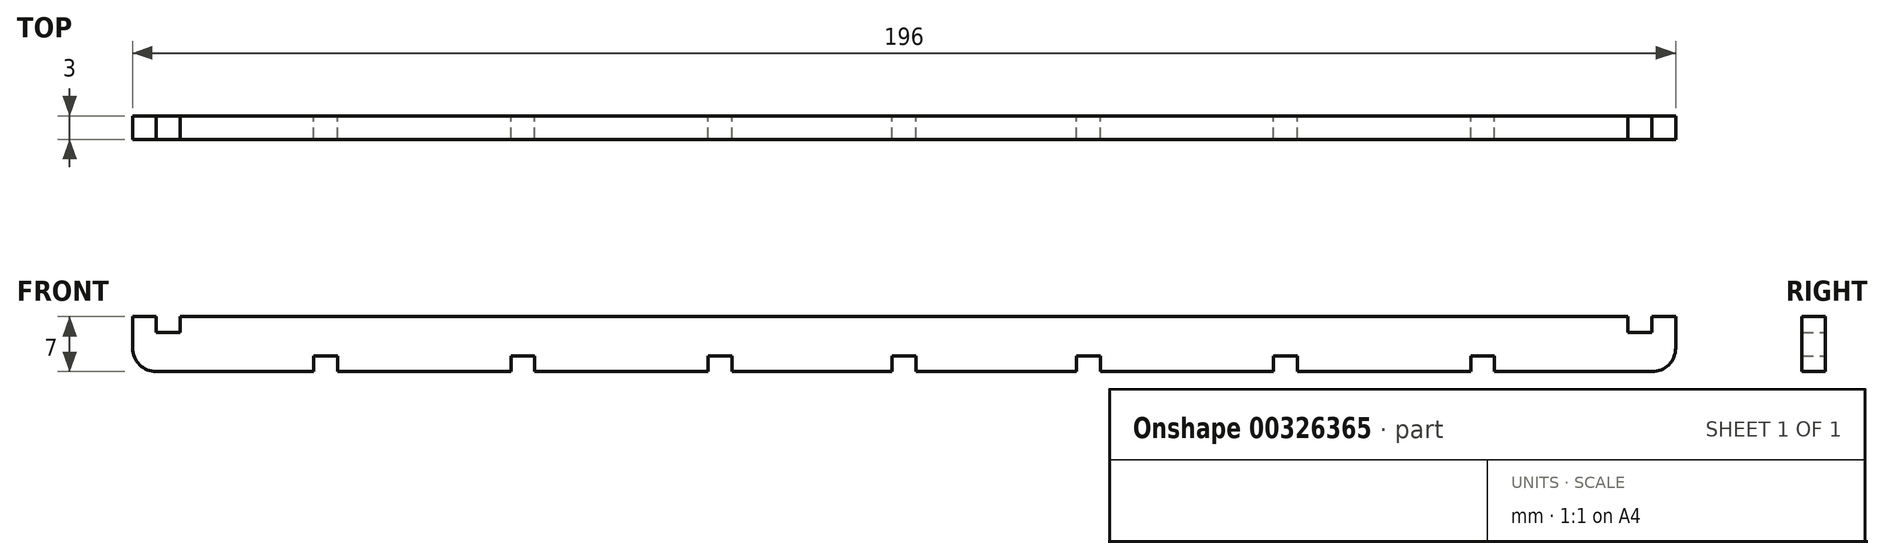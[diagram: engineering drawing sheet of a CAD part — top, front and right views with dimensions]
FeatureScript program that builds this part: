
annotation { "Feature Type Name" : "Feature", "Feature Type Description" : "" }
export const myFeature = defineFeature(function(context is Context, id is Id, definition is map)
    precondition{}
    {
        {
            var Q0;
            Q0=qCreatedBy(makeId("Front.planeOp"),FACE);
            var sketch = newSketch(context, id + "F0", { "sketchPlane" : qUnion([Q0])});
            skLineSegment(sketch, "E0", {"start": v(-71.96, 0) * mm, "end": v(-49.96, 0) * mm});
            skLineSegment(sketch, "E1", {"start": v(75, 2) * mm, "end": v(75, 0) * mm});
            skPoint(sketch, "E2", {"position": v(-75, 2) * mm});
            skLineSegment(sketch, "E3", {"start": v(-98, 7) * mm, "end": v(-98, 3) * mm});
            skLineSegment(sketch, "E4", {"start": v(-95, 5) * mm, "end": v(-91.96, 5) * mm});
            skLineSegment(sketch, "E5", {"start": v(-98, 7) * mm, "end": v(-95, 7) * mm});
            skLineSegment(sketch, "E6", {"start": v(-75, 2) * mm, "end": v(-75, 0) * mm});
            skLineSegment(sketch, "E7", {"start": v(-95, 7) * mm, "end": v(-95, 5) * mm});
            skLineSegment(sketch, "E8", {"start": v(-91.96, 5) * mm, "end": v(-91.96, 7) * mm});
            skLineSegment(sketch, "E9", {"start": v(-75, 2) * mm, "end": v(-71.96, 2) * mm});
            skLineSegment(sketch, "E10", {"start": v(-71.96, 2) * mm, "end": v(-71.96, 0) * mm});
            skLineSegment(sketch, "E11", {"start": v(-95, 0) * mm, "end": v(-75, 0) * mm});
            skLineSegment(sketch, "E12", {"start": v(71.96, 0) * mm, "end": v(71.96, 2) * mm});
            skLineSegment(sketch, "E13", {"start": v(71.96, 2) * mm, "end": v(75, 2) * mm});
            skLineSegment(sketch, "E14", {"start": v(75, 0) * mm, "end": v(95, 0) * mm});
            skLineSegment(sketch, "E15", {"start": v(98, 3) * mm, "end": v(98, 7) * mm});
            skLineSegment(sketch, "E16", {"start": v(98, 7) * mm, "end": v(95, 7) * mm});
            skLineSegment(sketch, "E17", {"start": v(95, 7) * mm, "end": v(95, 5) * mm});
            skLineSegment(sketch, "E18", {"start": v(95, 5) * mm, "end": v(91.96, 5) * mm});
            skLineSegment(sketch, "E19", {"start": v(91.96, 5) * mm, "end": v(91.96, 7) * mm});
            skPoint(sketch, "E20", {"position": v(-49.96, 0) * mm});
            skPoint(sketch, "E21", {"position": v(-24.92, 0) * mm});
            skPoint(sketch, "E22", {"position": v(24.92, 0) * mm});
            skPoint(sketch, "E23", {"position": v(49.96, 0) * mm});
            skLineSegment(sketch, "E24", {"start": v(-49.96, 0) * mm, "end": v(-49.96, 2) * mm});
            skLineSegment(sketch, "E25", {"start": v(-49.96, 2) * mm, "end": v(-46.92, 2) * mm});
            skLineSegment(sketch, "E26", {"start": v(-46.92, 2) * mm, "end": v(-46.92, 0) * mm});
            skLineSegment(sketch, "E27", {"start": v(-24.92, 0) * mm, "end": v(-24.92, 2) * mm});
            skLineSegment(sketch, "E28", {"start": v(-24.92, 2) * mm, "end": v(-21.88, 2) * mm});
            skLineSegment(sketch, "E29", {"start": v(-21.88, 2) * mm, "end": v(-21.88, 0) * mm});
            skLineSegment(sketch, "E30", {"start": v(24.92, 0) * mm, "end": v(24.92, 2) * mm});
            skLineSegment(sketch, "E31", {"start": v(24.92, 2) * mm, "end": v(21.88, 2) * mm});
            skLineSegment(sketch, "E32", {"start": v(21.88, 2) * mm, "end": v(21.88, 0) * mm});
            skLineSegment(sketch, "E33", {"start": v(49.96, 0) * mm, "end": v(49.96, 2) * mm});
            skLineSegment(sketch, "E34", {"start": v(49.96, 2) * mm, "end": v(46.92, 2) * mm});
            skLineSegment(sketch, "E35", {"start": v(46.92, 2) * mm, "end": v(46.92, 0) * mm});
            skPoint(sketch, "E36", {"position": v(-1.52, 0) * mm});
            skPoint(sketch, "E37", {"position": v(1.52, 0) * mm});
            skLineSegment(sketch, "E38", {"start": v(-1.52, 0) * mm, "end": v(-1.52, 2) * mm});
            skLineSegment(sketch, "E39", {"start": v(-1.52, 2) * mm, "end": v(1.52, 2) * mm});
            skLineSegment(sketch, "E40", {"start": v(1.52, 2) * mm, "end": v(1.52, 0) * mm});
            skLineSegment(sketch, "E41.trimOffspring", {"start": v(-46.92, 0) * mm, "end": v(-24.92, 0) * mm});
            skLineSegment(sketch, "E42.trimOffspring", {"start": v(-21.88, 0) * mm, "end": v(-1.52, 0) * mm});
            skLineSegment(sketch, "E43.trimOffspring", {"start": v(1.52, 0) * mm, "end": v(21.88, 0) * mm});
            skLineSegment(sketch, "E44.trimOffspring", {"start": v(24.92, 0) * mm, "end": v(46.92, 0) * mm});
            skLineSegment(sketch, "E45.trimOffspring", {"start": v(49.96, 0) * mm, "end": v(71.96, 0) * mm});
            skPoint(sketch, "E46.visualSharp", {"position": v(-98, 0) * mm});
            skArc(sketch, "E46.filletArc", {"start": v(-98, 3) * mm, "mid": v(-97.12, 0.88) * mm, "end": v(-95, 0) * mm});
            skPoint(sketch, "E47.visualSharp", {"position": v(98, 0) * mm});
            skArc(sketch, "E47.filletArc", {"start": v(95, 0) * mm, "mid": v(97.12, 0.88) * mm, "end": v(98, 3) * mm});
            skLineSegment(sketch, "E48", {"start": v(-91.96, 7) * mm, "end": v(91.96, 7) * mm});
            skSolve(sketch);
        }
        {
            var Q0;
            Q0=makeQuery(id+"F0.imprint","IMPRINT",FACE,{"disambiguationData":[TD([[makeQuery(id+"F0.imprint","IMPRINT",EDGE,{"derivedFrom":sQuery(id+"F0.wireOp",EDGE,"E0")}),1.0]])]});
            extrude(context, id + "F1", {"entities" : qUnion([Q0]), "depth" : 3 * mm});
        }
    });
